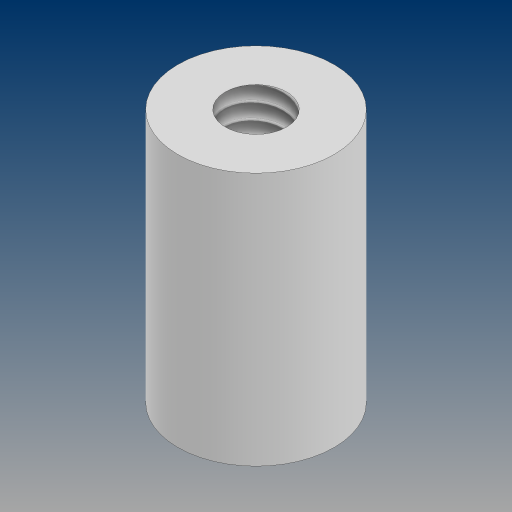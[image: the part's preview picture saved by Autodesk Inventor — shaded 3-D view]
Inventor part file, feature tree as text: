
AUTODESK INVENTOR PART (.ipt)
format: ipt  version: 2024.3 (Build 283343000, 343)  size: 97,792 bytes
history: native  units: in
note: dims shown in document units (in); Inventor stores cm internally (conversion verified against a paired STEP export)
features: sketch x2, extrude x1, hole x1
ambient origin geometry x8: Origin, YZ Plane, XZ Plane, XY Plane, X Axis, Y Axis, Z Axis, Center Point
bodies: Solid1 (feature_tree)
feature tree (4):
  extrude  "Extrusion1"  Depth=0.813in TaperAngle=0.0deg
  hole  "Hole1"  [1 undecoded]
  sketch  "Sketch1"  dims[d0=0.5in d1=0.813in d2=0.0in]
  sketch  "Sketch2"  dims[d3=0.196in d4=1.0in d5=0.375in d6=0.25in d7=0.5635in d8=1.0in d9=0.8108in]
note: 1 required parameter value undecoded (feature->parameter linkage not recoverable at this tier; creation-order binding heuristic only, values carry confidence <= 0.55)
